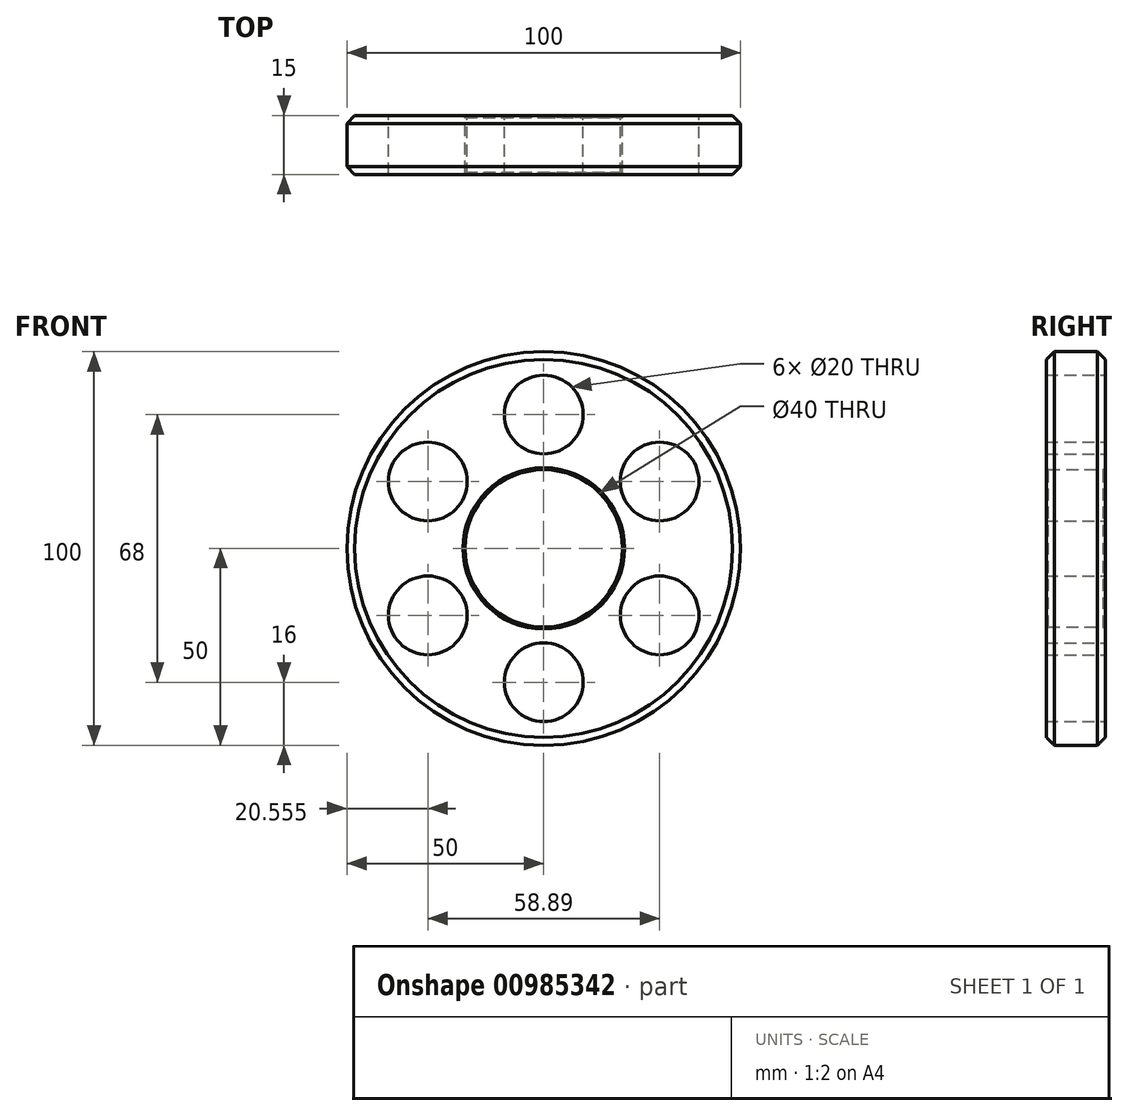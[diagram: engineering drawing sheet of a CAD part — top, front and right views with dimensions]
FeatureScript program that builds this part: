
annotation { "Feature Type Name" : "Feature", "Feature Type Description" : "" }
export const myFeature = defineFeature(function(context is Context, id is Id, definition is map)
    precondition{}
    {
        {
            var Q0;
            Q0=qCreatedBy(makeId("Front.planeOp"),FACE);
            var sketch = newSketch(context, id + "F0", { "sketchPlane" : qUnion([Q0])});
            skCircle(sketch, "E0", {"center": v(0, 0) * mm, "radius": 50 * mm});
            skCircle(sketch, "E1", {"center": v(0, 34) * mm, "radius": 10 * mm});
            skCircle(sketch, "E2", {"center": v(0, 34) * mm, "radius": 8 * mm});
            skCircle(sketch, "E3", {"center": v(0, 0) * mm, "radius": 20 * mm});
            skCircle(sketch, "E4.1.0", {"center": v(-29.44, 17) * mm, "radius": 10 * mm});
            skCircle(sketch, "E4.1.1", {"center": v(-29.44, 17) * mm, "radius": 8 * mm});
            skCircle(sketch, "E4.2.0", {"center": v(-29.44, -17) * mm, "radius": 10 * mm});
            skCircle(sketch, "E4.2.1", {"center": v(-29.44, -17) * mm, "radius": 8 * mm});
            skCircle(sketch, "E4.3.0", {"center": v(0, -34) * mm, "radius": 10 * mm});
            skCircle(sketch, "E4.3.1", {"center": v(0, -34) * mm, "radius": 8 * mm});
            skCircle(sketch, "E4.4.0", {"center": v(29.44, -17) * mm, "radius": 10 * mm});
            skCircle(sketch, "E4.4.1", {"center": v(29.44, -17) * mm, "radius": 8 * mm});
            skCircle(sketch, "E4.5.0", {"center": v(29.44, 17) * mm, "radius": 10 * mm});
            skCircle(sketch, "E4.5.1", {"center": v(29.44, 17) * mm, "radius": 8 * mm});
            skSolve(sketch);
        }
        {
            var Q0;
            Q0=makeQuery(id+"F0.imprint","IMPRINT",FACE,{"disambiguationData":[TD([[makeQuery(id+"F0.imprint","IMPRINT",EDGE,{"derivedFrom":sQuery(id+"F0.wireOp",EDGE,"E0")}),1.0]])]});
            extrude(context, id + "F1", {"entities" : qUnion([Q0]), "endBound" : BoundingType.SYMMETRIC, "depth" : 15 * mm});
        }
        {
            var Q0;
            Q0=makeQuery(id+"F1.opExtrude","CAP_EDGE",EDGE,{"disambiguationData":[OSD([sQuery(id+"F0.wireOp",EDGE,"E0")])],"isStart":false});
            var Q1;
            Q1=makeQuery(id+"F1.opExtrude","CAP_EDGE",EDGE,{"disambiguationData":[OSD([sQuery(id+"F0.wireOp",EDGE,"E0")])],"isStart":true});
            chamfer(context, id + "F2", {"entities" : qUnion([Q0, Q1]), "width" : 2 * mm, "tangentPropagation" : true});
        }
        {
            var Q0;
            Q0=makeQuery(id+"F1.opExtrude","CAP_EDGE",EDGE,{"disambiguationData":[OSD([sQuery(id+"F0.wireOp",EDGE,"E3")])],"isStart":false});
            var Q1;
            Q1=makeQuery(id+"F1.opExtrude","CAP_EDGE",EDGE,{"disambiguationData":[OSD([sQuery(id+"F0.wireOp",EDGE,"E3")])],"isStart":true});
            chamfer(context, id + "F3", {"entities" : qUnion([Q0, Q1]), "width" : 0.5 * mm, "tangentPropagation" : true});
        }
    });
